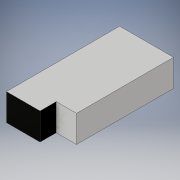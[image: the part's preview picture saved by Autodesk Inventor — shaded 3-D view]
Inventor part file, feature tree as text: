
AUTODESK INVENTOR PART (.ipt)
format: ipt  version: 2019.4 (Build 234330000, 330)  size: 99,328 bytes
history: native  units: mm
features: extrude x2, sketch x2
ambient origin geometry x8: Origin, YZ Plane, XZ Plane, XY Plane, X Axis, Y Axis, Z Axis, Center Point
bodies: Solid1 (feature_tree)
feature tree (4):
  extrude  "Extrusion1"  Depth=228.6mm
  extrude  "Extrusion2"  Depth=79.2mm
  sketch  "Sketch1"  dims[d0=127.0mm d1=228.6mm]
  sketch  "Sketch2"  dims[d2=63.5mm d3=0.0mm d4=79.2mm d5=38.1mm d6=0.0mm]
